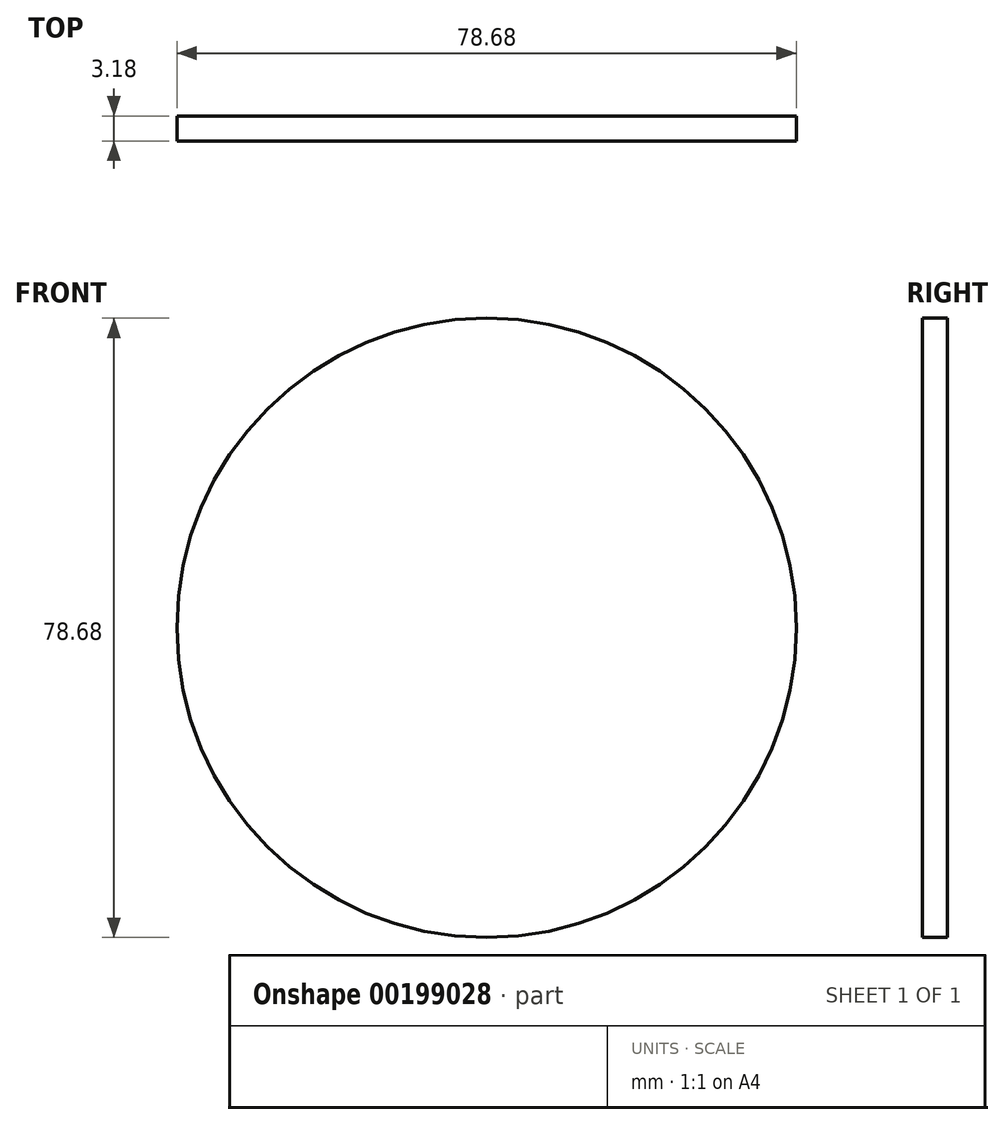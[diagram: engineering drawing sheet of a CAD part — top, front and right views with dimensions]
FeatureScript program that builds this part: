
annotation { "Feature Type Name" : "Feature", "Feature Type Description" : "" }
export const myFeature = defineFeature(function(context is Context, id is Id, definition is map)
    precondition{}
    {
        {
            var Q0;
            Q0=qCreatedBy(makeId("Front.planeOp"),FACE);
            var sketch = newSketch(context, id + "F0", { "sketchPlane" : qUnion([Q0])});
            skCircle(sketch, "E0", {"center": v(0, 0) * mm, "radius": 39.34 * mm});
            skSolve(sketch);
        }
        {
            var Q0;
            Q0=makeQuery(id+"F0.imprint","IMPRINT",FACE,{"disambiguationData":[TD([[makeQuery(id+"F0.imprint","IMPRINT",EDGE,{"derivedFrom":sQuery(id+"F0.wireOp",EDGE,"E0")}),1.0]])]});
            extrude(context, id + "F1", {"entities" : qUnion([Q0]), "oppositeDirection" : true, "depth" : 3.17 * mm});
        }
    });
